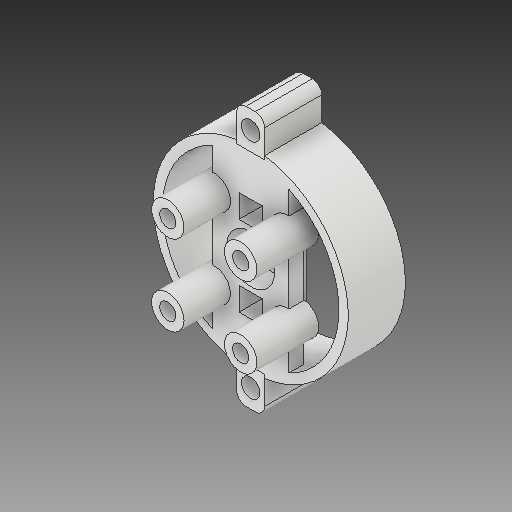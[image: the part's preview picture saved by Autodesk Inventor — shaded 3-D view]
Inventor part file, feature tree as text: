
AUTODESK INVENTOR PART (.ipt)
format: ipt  version: 2018 (Build 220112000, 112)  size: 208,896 bytes
history: native  units: in
note: dims shown in document units (in); Inventor stores cm internally (conversion verified against a paired STEP export)
features: mirror x1
ambient origin geometry x8: Origin, YZ Plane, XZ Plane, XY Plane, X Axis, Y Axis, Z Axis, Center Point
bodies: Solid1 (feature_tree)
feature tree (1):
  mirror  "Mirror7"
